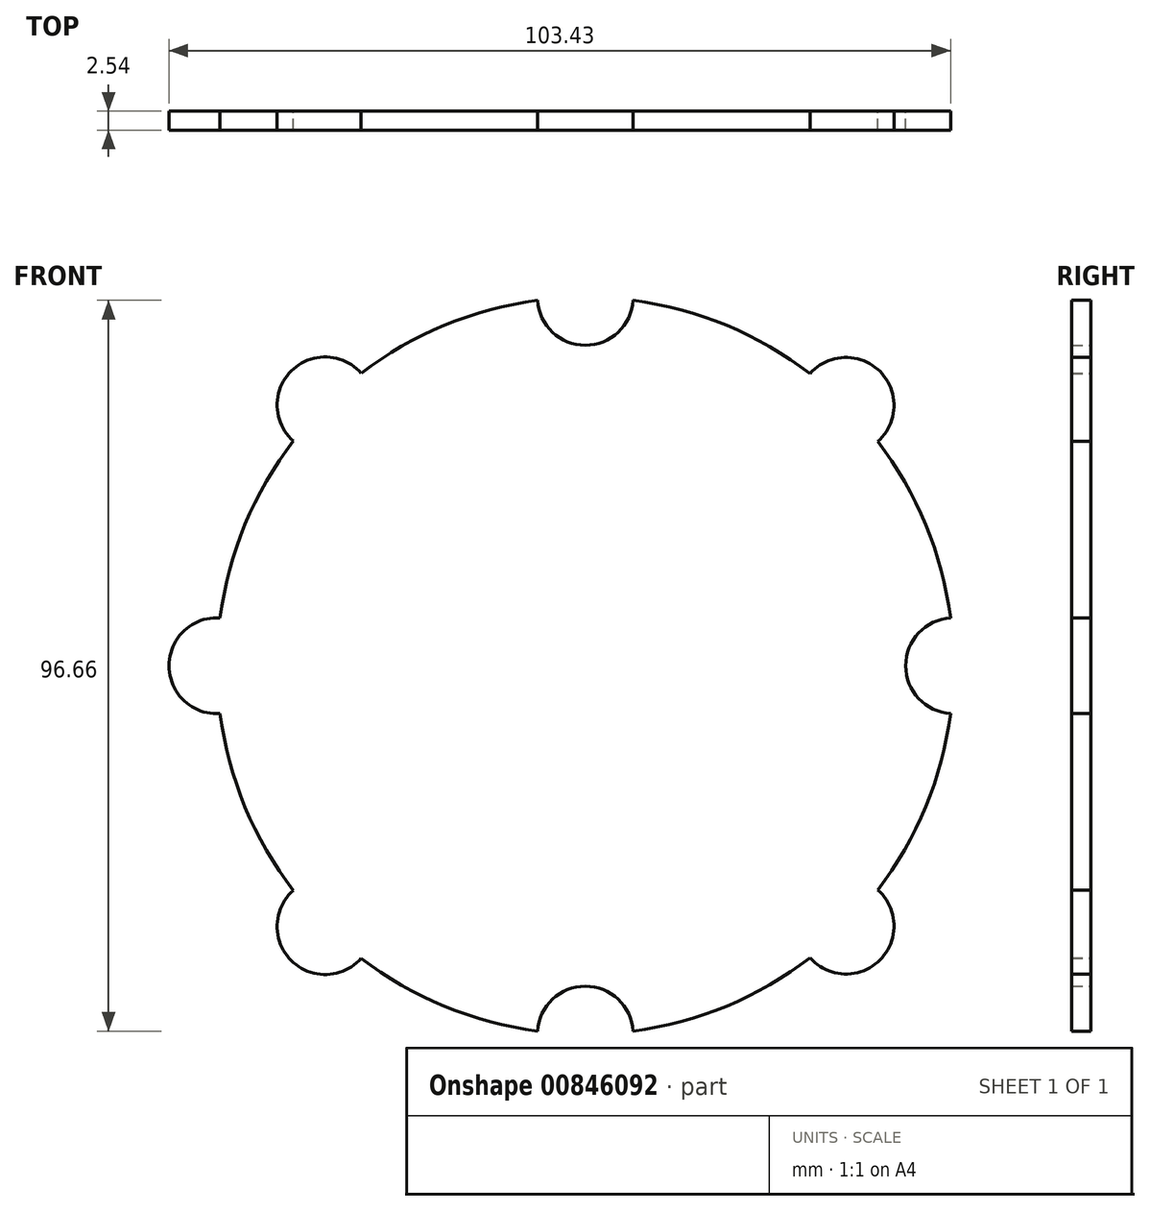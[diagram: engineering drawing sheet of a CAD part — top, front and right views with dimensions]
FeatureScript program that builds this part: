
annotation { "Feature Type Name" : "Feature", "Feature Type Description" : "" }
export const myFeature = defineFeature(function(context is Context, id is Id, definition is map)
    precondition{}
    {
        {
            var Q0;
            Q0=qCreatedBy(makeId("Front.planeOp"),FACE);
            var sketch = newSketch(context, id + "F0", { "sketchPlane" : qUnion([Q0])});
            skLineSegment(sketch, "E0", {"start": v(-58.74, 0) * mm, "end": v(58.41, 0) * mm, "construction": true});
            skLineSegment(sketch, "E1", {"start": v(0, -58.33) * mm, "end": v(0, 59.96) * mm, "construction": true});
            skCircle(sketch, "E2", {"center": v(0, 0) * mm, "radius": 7.28 * mm});
            skLineSegment(sketch, "E3", {"start": v(-46.58, -46.63) * mm, "end": v(53.05, 53) * mm, "construction": true});
            skLineSegment(sketch, "E4", {"start": v(48.28, -48.21) * mm, "end": v(-55.79, 55.85) * mm, "construction": true});
            skCircle(sketch, "E5", {"center": v(0, 48.75) * mm, "radius": 6.35 * mm});
            skCircle(sketch, "E6", {"center": v(0, 0) * mm, "radius": 48.75 * mm});
            skCircle(sketch, "E7", {"center": v(34.5, 34.44) * mm, "radius": 6.35 * mm});
            skCircle(sketch, "E8", {"center": v(48.75, 0) * mm, "radius": 6.35 * mm});
            skCircle(sketch, "E9", {"center": v(34.5, -34.44) * mm, "radius": 6.35 * mm});
            skCircle(sketch, "E10", {"center": v(0, -48.75) * mm, "radius": 6.35 * mm});
            skCircle(sketch, "E11", {"center": v(-34.44, -34.5) * mm, "radius": 6.35 * mm});
            skCircle(sketch, "E12", {"center": v(-48.75, 0) * mm, "radius": 6.35 * mm});
            skCircle(sketch, "E13", {"center": v(-34.44, 34.5) * mm, "radius": 6.35 * mm});
            skSolve(sketch);
        }
        {
            var Q0;
            {var subQ0=sQuery(id+"F0.wireOp",EDGE,"E13");var subQ1=sQuery(id+"F0.wireOp",EDGE,"E6");var subQ2=makeQuery(id+"F0.imprint","INTERSECT",VERTEX,{"disambiguationData":[OD(0.0)],"derivedFrom":[subQ1,subQ0]});Q0=makeQuery(id+"F0.imprint","IMPRINT",FACE,{"disambiguationData":[TD([[makeQuery(id+"F0.imprint","IMPRINT",EDGE,{"disambiguationData":[TD([[subQ2,-1.0]])],"derivedFrom":subQ1}),-1.0]])]});}
            var Q1;
            {var subQ0=sQuery(id+"F0.wireOp",EDGE,"E13");var subQ1=sQuery(id+"F0.wireOp",EDGE,"E6");var subQ2=makeQuery(id+"F0.imprint","INTERSECT",VERTEX,{"disambiguationData":[OD(0.0)],"derivedFrom":[subQ1,subQ0]});Q1=makeQuery(id+"F0.imprint","IMPRINT",FACE,{"disambiguationData":[TD([[makeQuery(id+"F0.imprint","IMPRINT",EDGE,{"disambiguationData":[TD([[subQ2,-1.0]])],"derivedFrom":subQ1}),1.0]])]});}
            var Q2;
            {var subQ0=sQuery(id+"F0.wireOp",EDGE,"E6");var subQ1=sQuery(id+"F0.wireOp",EDGE,"E5");var subQ2=makeQuery(id+"F0.imprint","INTERSECT",VERTEX,{"disambiguationData":[OD(0.0)],"derivedFrom":[subQ1,subQ0]});Q2=makeQuery(id+"F0.imprint","IMPRINT",FACE,{"disambiguationData":[TD([[makeQuery(id+"F0.imprint","IMPRINT",EDGE,{"disambiguationData":[TD([[subQ2,-1.0]])],"derivedFrom":subQ1}),-1.0]])]});}
            var Q3;
            {var subQ0=sQuery(id+"F0.wireOp",EDGE,"E6");var subQ1=sQuery(id+"F0.wireOp",EDGE,"E5");var subQ2=makeQuery(id+"F0.imprint","INTERSECT",VERTEX,{"disambiguationData":[OD(0.0)],"derivedFrom":[subQ1,subQ0]});Q3=makeQuery(id+"F0.imprint","IMPRINT",FACE,{"disambiguationData":[TD([[makeQuery(id+"F0.imprint","IMPRINT",EDGE,{"disambiguationData":[TD([[subQ2,1.0]])],"derivedFrom":subQ1}),-1.0]])]});}
            var Q4;
            {var subQ0=sQuery(id+"F0.wireOp",EDGE,"E7");var subQ1=sQuery(id+"F0.wireOp",EDGE,"E6");var subQ2=makeQuery(id+"F0.imprint","INTERSECT",VERTEX,{"disambiguationData":[OD(0.0)],"derivedFrom":[subQ1,subQ0]});Q4=makeQuery(id+"F0.imprint","IMPRINT",FACE,{"disambiguationData":[TD([[makeQuery(id+"F0.imprint","IMPRINT",EDGE,{"disambiguationData":[TD([[subQ2,-1.0]])],"derivedFrom":subQ1}),1.0]])]});}
            var Q5;
            {var subQ0=sQuery(id+"F0.wireOp",EDGE,"E7");var subQ1=sQuery(id+"F0.wireOp",EDGE,"E6");var subQ2=makeQuery(id+"F0.imprint","INTERSECT",VERTEX,{"disambiguationData":[OD(0.0)],"derivedFrom":[subQ1,subQ0]});Q5=makeQuery(id+"F0.imprint","IMPRINT",FACE,{"disambiguationData":[TD([[makeQuery(id+"F0.imprint","IMPRINT",EDGE,{"disambiguationData":[TD([[subQ2,-1.0]])],"derivedFrom":subQ1}),-1.0]])]});}
            var Q6;
            Q6=makeQuery(id+"F0.imprint","IMPRINT",FACE,{"disambiguationData":[TD([[makeQuery(id+"F0.imprint","IMPRINT",EDGE,{"derivedFrom":sQuery(id+"F0.wireOp",EDGE,"E2")}),1.0]])]});
            var Q7;
            {var subQ0=sQuery(id+"F0.wireOp",EDGE,"E8");var subQ1=sQuery(id+"F0.wireOp",EDGE,"E6");var subQ2=makeQuery(id+"F0.imprint","INTERSECT",VERTEX,{"disambiguationData":[OD(0.0)],"derivedFrom":[subQ1,subQ0]});Q7=makeQuery(id+"F0.imprint","IMPRINT",FACE,{"disambiguationData":[TD([[makeQuery(id+"F0.imprint","IMPRINT",EDGE,{"disambiguationData":[TD([[subQ2,1.0]])],"derivedFrom":subQ1}),-1.0]])]});}
            var Q8;
            {var subQ0=sQuery(id+"F0.wireOp",EDGE,"E8");var subQ1=sQuery(id+"F0.wireOp",EDGE,"E6");var subQ2=makeQuery(id+"F0.imprint","INTERSECT",VERTEX,{"disambiguationData":[OD(0.0)],"derivedFrom":[subQ1,subQ0]});Q8=makeQuery(id+"F0.imprint","IMPRINT",FACE,{"disambiguationData":[TD([[makeQuery(id+"F0.imprint","IMPRINT",EDGE,{"disambiguationData":[TD([[subQ2,1.0]])],"derivedFrom":subQ1}),1.0]])]});}
            var Q9;
            {var subQ0=sQuery(id+"F0.wireOp",EDGE,"E9");var subQ1=sQuery(id+"F0.wireOp",EDGE,"E6");var subQ2=makeQuery(id+"F0.imprint","INTERSECT",VERTEX,{"disambiguationData":[OD(0.0)],"derivedFrom":[subQ1,subQ0]});Q9=makeQuery(id+"F0.imprint","IMPRINT",FACE,{"disambiguationData":[TD([[makeQuery(id+"F0.imprint","IMPRINT",EDGE,{"disambiguationData":[TD([[subQ2,-1.0]])],"derivedFrom":subQ1}),-1.0]])]});}
            var Q10;
            {var subQ0=sQuery(id+"F0.wireOp",EDGE,"E9");var subQ1=sQuery(id+"F0.wireOp",EDGE,"E6");var subQ2=makeQuery(id+"F0.imprint","INTERSECT",VERTEX,{"disambiguationData":[OD(0.0)],"derivedFrom":[subQ1,subQ0]});Q10=makeQuery(id+"F0.imprint","IMPRINT",FACE,{"disambiguationData":[TD([[makeQuery(id+"F0.imprint","IMPRINT",EDGE,{"disambiguationData":[TD([[subQ2,-1.0]])],"derivedFrom":subQ1}),1.0]])]});}
            var Q11;
            {var subQ0=sQuery(id+"F0.wireOp",EDGE,"E10");var subQ1=sQuery(id+"F0.wireOp",EDGE,"E6");var subQ2=makeQuery(id+"F0.imprint","INTERSECT",VERTEX,{"disambiguationData":[OD(0.0)],"derivedFrom":[subQ1,subQ0]});Q11=makeQuery(id+"F0.imprint","IMPRINT",FACE,{"disambiguationData":[TD([[makeQuery(id+"F0.imprint","IMPRINT",EDGE,{"disambiguationData":[TD([[subQ2,-1.0]])],"derivedFrom":subQ1}),-1.0]])]});}
            var Q12;
            {var subQ0=sQuery(id+"F0.wireOp",EDGE,"E10");var subQ1=sQuery(id+"F0.wireOp",EDGE,"E6");var subQ2=makeQuery(id+"F0.imprint","INTERSECT",VERTEX,{"disambiguationData":[OD(0.0)],"derivedFrom":[subQ1,subQ0]});Q12=makeQuery(id+"F0.imprint","IMPRINT",FACE,{"disambiguationData":[TD([[makeQuery(id+"F0.imprint","IMPRINT",EDGE,{"disambiguationData":[TD([[subQ2,-1.0]])],"derivedFrom":subQ1}),1.0]])]});}
            var Q13;
            {var subQ0=sQuery(id+"F0.wireOp",EDGE,"E11");var subQ1=sQuery(id+"F0.wireOp",EDGE,"E6");var subQ2=makeQuery(id+"F0.imprint","INTERSECT",VERTEX,{"disambiguationData":[OD(0.0)],"derivedFrom":[subQ1,subQ0]});Q13=makeQuery(id+"F0.imprint","IMPRINT",FACE,{"disambiguationData":[TD([[makeQuery(id+"F0.imprint","IMPRINT",EDGE,{"disambiguationData":[TD([[subQ2,-1.0]])],"derivedFrom":subQ1}),-1.0]])]});}
            var Q14;
            {var subQ0=sQuery(id+"F0.wireOp",EDGE,"E11");var subQ1=sQuery(id+"F0.wireOp",EDGE,"E6");var subQ2=makeQuery(id+"F0.imprint","INTERSECT",VERTEX,{"disambiguationData":[OD(0.0)],"derivedFrom":[subQ1,subQ0]});Q14=makeQuery(id+"F0.imprint","IMPRINT",FACE,{"disambiguationData":[TD([[makeQuery(id+"F0.imprint","IMPRINT",EDGE,{"disambiguationData":[TD([[subQ2,-1.0]])],"derivedFrom":subQ1}),1.0]])]});}
            var Q15;
            {var subQ0=sQuery(id+"F0.wireOp",EDGE,"E12");var subQ1=sQuery(id+"F0.wireOp",EDGE,"E6");var subQ2=makeQuery(id+"F0.imprint","INTERSECT",VERTEX,{"disambiguationData":[OD(0.0)],"derivedFrom":[subQ1,subQ0]});Q15=makeQuery(id+"F0.imprint","IMPRINT",FACE,{"disambiguationData":[TD([[makeQuery(id+"F0.imprint","IMPRINT",EDGE,{"disambiguationData":[TD([[subQ2,-1.0]])],"derivedFrom":subQ1}),-1.0]])]});}
            var Q16;
            {var subQ0=sQuery(id+"F0.wireOp",EDGE,"E12");var subQ1=sQuery(id+"F0.wireOp",EDGE,"E6");var subQ2=makeQuery(id+"F0.imprint","INTERSECT",VERTEX,{"disambiguationData":[OD(0.0)],"derivedFrom":[subQ1,subQ0]});Q16=makeQuery(id+"F0.imprint","IMPRINT",FACE,{"disambiguationData":[TD([[makeQuery(id+"F0.imprint","IMPRINT",EDGE,{"disambiguationData":[TD([[subQ2,-1.0]])],"derivedFrom":subQ1}),1.0]])]});}
            extrude(context, id + "F1", {"entities" : qUnion([Q0, Q1, Q2, Q3, Q4, Q5, Q6, Q7, Q8, Q9, Q10, Q11, Q12, Q13, Q14, Q15, Q16]), "depth" : 2.54 * mm, "offsetDistance" : 25.4 * mm});
        }
    });
